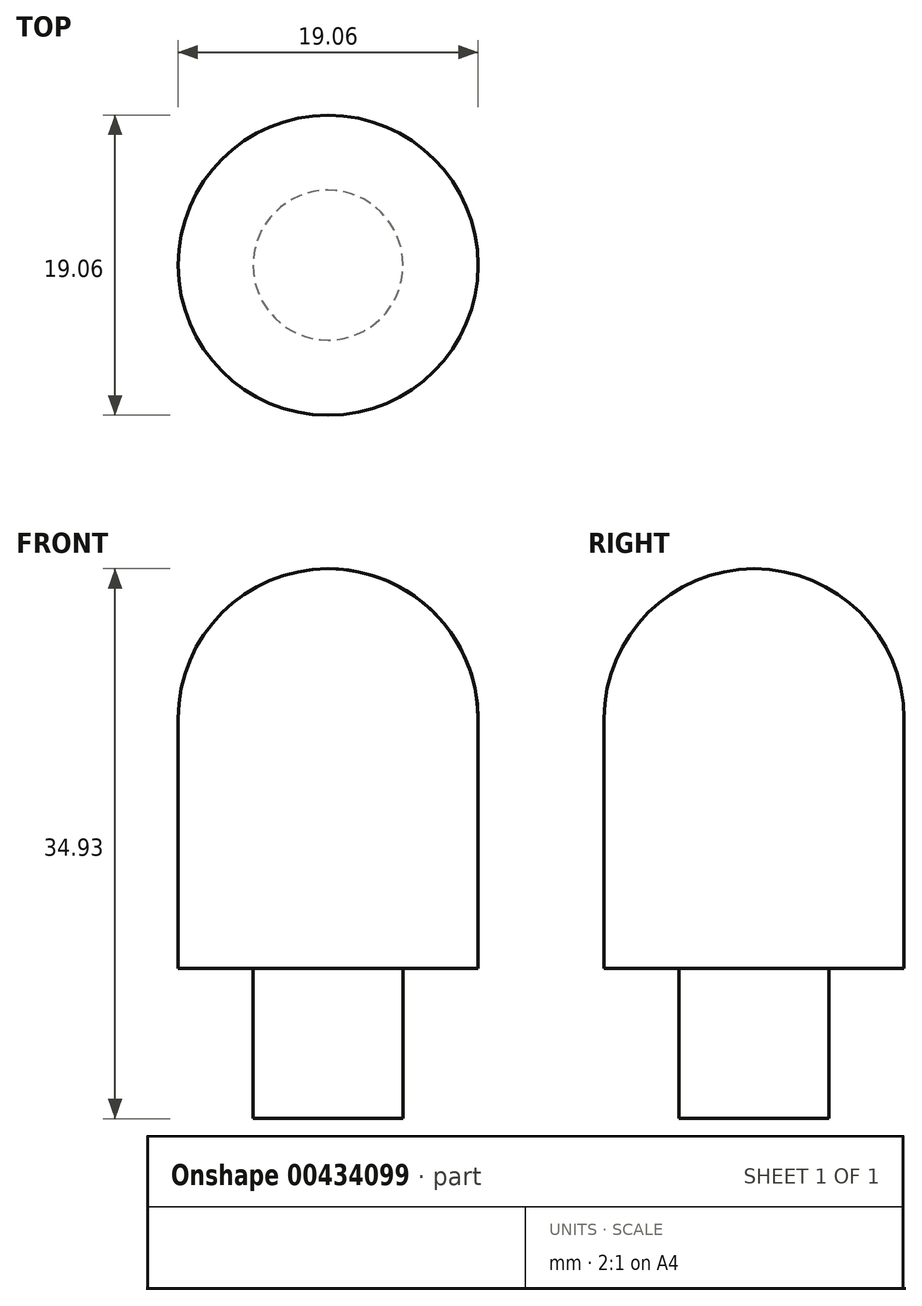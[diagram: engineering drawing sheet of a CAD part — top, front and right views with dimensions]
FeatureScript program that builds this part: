
annotation { "Feature Type Name" : "Feature", "Feature Type Description" : "" }
export const myFeature = defineFeature(function(context is Context, id is Id, definition is map)
    precondition{}
    {
        {
            var Q0;
            Q0=qCreatedBy(makeId("Front.planeOp"),FACE);
            var sketch = newSketch(context, id + "F0", { "sketchPlane" : qUnion([Q0])});
            skArc(sketch, "E0", {"start": v(0, 25.4) * mm, "mid": v(-6.74, 22.61) * mm, "end": v(-9.52, 15.88) * mm});
            skLineSegment(sketch, "E1", {"start": v(-9.52, 15.88) * mm, "end": v(-9.52, 0) * mm});
            skLineSegment(sketch, "E2", {"start": v(-9.52, 0) * mm, "end": v(-4.76, 0) * mm});
            skLineSegment(sketch, "E3", {"start": v(-4.76, 0) * mm, "end": v(-4.76, -9.53) * mm});
            skLineSegment(sketch, "E4", {"start": v(-4.76, -9.53) * mm, "end": v(0, -9.53) * mm});
            skLineSegment(sketch, "E5", {"start": v(0, -9.53) * mm, "end": v(0, 25.4) * mm});
            skSolve(sketch);
        }
        {
            var Q0;
            Q0=makeQuery(id+"F0.imprint","IMPRINT",FACE,{"disambiguationData":[TD([[makeQuery(id+"F0.imprint","IMPRINT",EDGE,{"derivedFrom":sQuery(id+"F0.wireOp",EDGE,"E0")}),1.0]])]});
            var Q1;
            Q1=sQuery(id+"F0.wireOp",EDGE,"E5");
            revolve(context, id + "F1", {"entities" : qUnion([Q0]), "axis" : qUnion([Q1]), "revolveType" : RevolveType.FULL});
        }
    });
